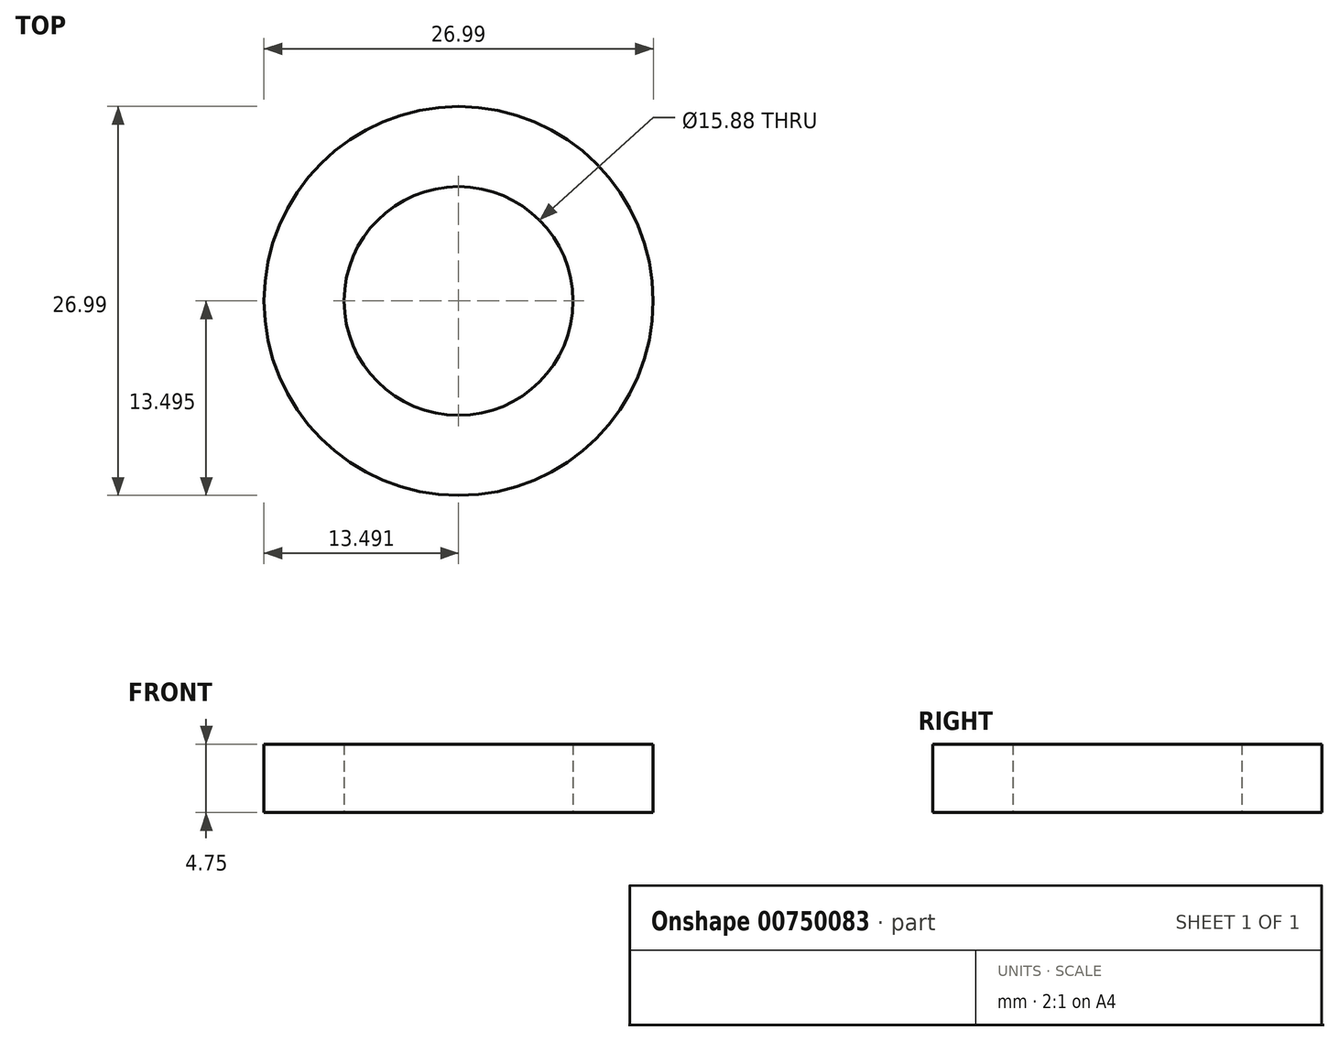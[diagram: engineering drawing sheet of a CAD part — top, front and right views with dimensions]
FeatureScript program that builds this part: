
annotation { "Feature Type Name" : "Feature", "Feature Type Description" : "" }
export const myFeature = defineFeature(function(context is Context, id is Id, definition is map)
    precondition{}
    {
        {
            var Q0;
            Q0=qCreatedBy(makeId("Top.planeOp"),FACE);
            var sketch = newSketch(context, id + "F0", { "sketchPlane" : qUnion([Q0])});
            skCircle(sketch, "E0", {"center": v(-39.22, 31.95) * mm, "radius": 13.5 * mm});
            skCircle(sketch, "E1", {"center": v(-39.22, 31.95) * mm, "radius": 7.94 * mm});
            skSolve(sketch);
        }
        {
            var Q0;
            Q0=makeQuery(id+"F0.imprint","IMPRINT",FACE,{"disambiguationData":[TD([[makeQuery(id+"F0.imprint","IMPRINT",EDGE,{"derivedFrom":sQuery(id+"F0.wireOp",EDGE,"E0")}),1.0]])]});
            extrude(context, id + "F1", {"entities" : qUnion([Q0]), "depth" : 4.75 * mm, "offsetDistance" : 25.4 * mm});
        }
    });
